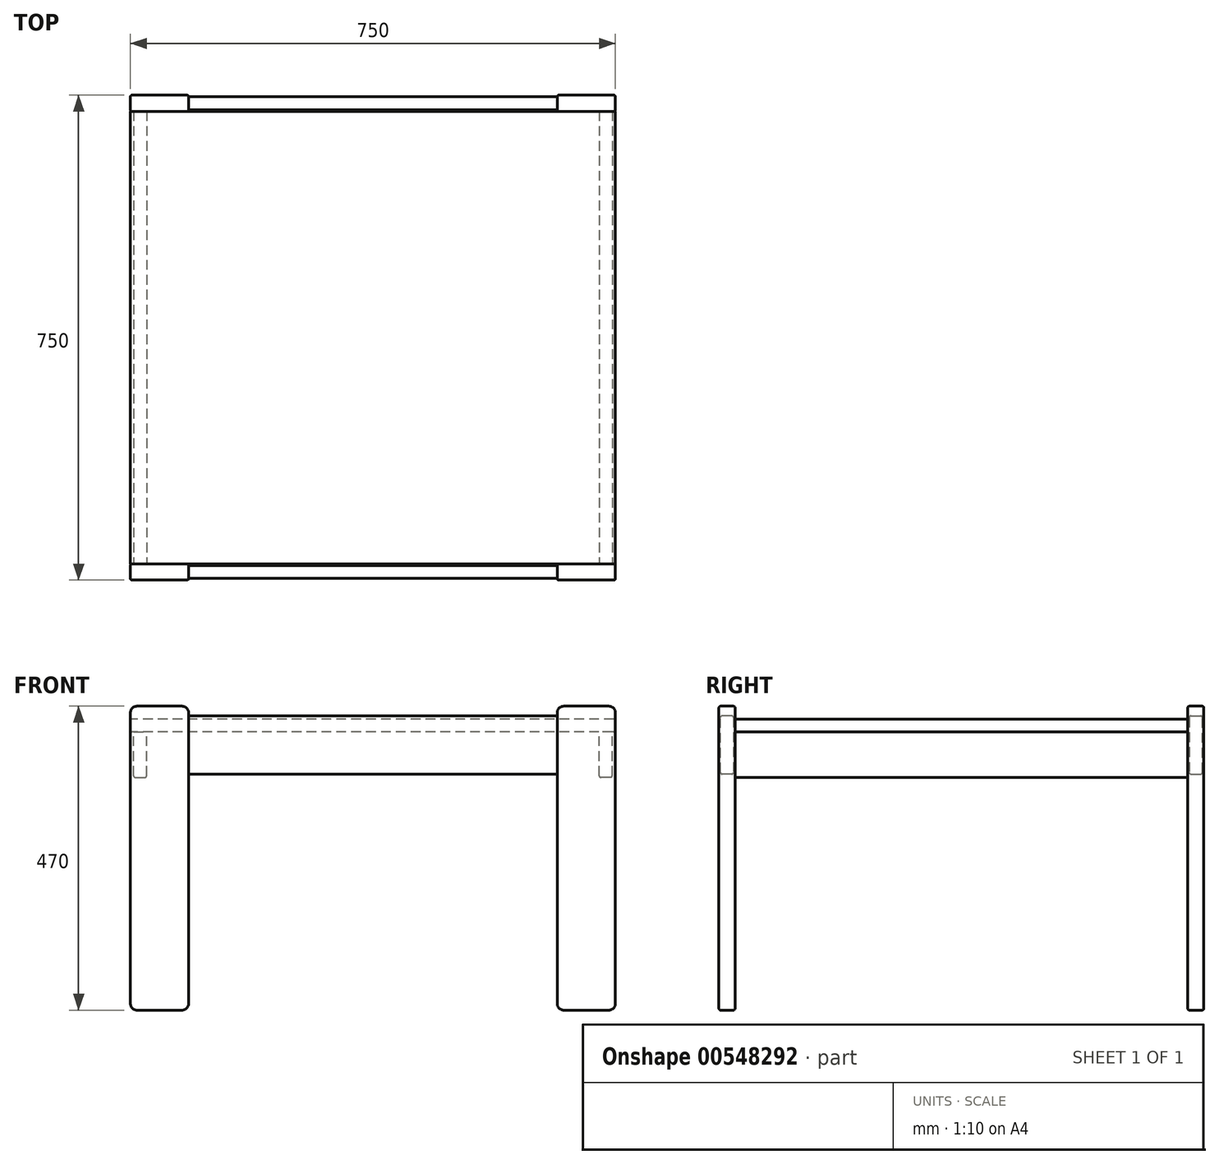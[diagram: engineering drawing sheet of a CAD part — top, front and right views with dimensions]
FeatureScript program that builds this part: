
annotation { "Feature Type Name" : "Feature", "Feature Type Description" : "" }
export const myFeature = defineFeature(function(context is Context, id is Id, definition is map)
    precondition{}
    {
        {
            var Q0;
            Q0=qCreatedBy(makeId("Top.planeOp"),FACE);
            var sketch = newSketch(context, id + "F0", { "sketchPlane" : qUnion([Q0])});
            skLineSegment(sketch, "E0.bottom", {"start": v(375, 350) * mm, "end": v(-375, 350) * mm});
            skLineSegment(sketch, "E0.top", {"start": v(375, -350) * mm, "end": v(-375, -350) * mm});
            skLineSegment(sketch, "E0.left", {"start": v(375, 350) * mm, "end": v(375, -350) * mm});
            skLineSegment(sketch, "E0.right", {"start": v(-375, 350) * mm, "end": v(-375, -350) * mm});
            skPoint(sketch, "E0.middle", {"position": v(0, 0) * mm});
            skSolve(sketch);
        }
        {
            var Q0;
            Q0 = qSketchRegion(id + "F0", true);
            extrude(context, id + "F1", {"entities" : qUnion([Q0]), "oppositeDirection" : true, "depth" : 20 * mm, "offsetDistance" : 25 * mm});
        }
        {
            var Q0;
            Q0=makeQuery(id+"F1.opExtrude","SWEPT_FACE",FACE,{"disambiguationData":[OSD([sQuery(id+"F0.wireOp",EDGE,"E0.top")])]});
            var sketch = newSketch(context, id + "F2", { "sketchPlane" : qUnion([Q0])});
            skLineSegment(sketch, "E1.bottom", {"start": v(375, 20) * mm, "end": v(285, 20) * mm});
            skLineSegment(sketch, "E1.top", {"start": v(375, -450) * mm, "end": v(285, -450) * mm});
            skLineSegment(sketch, "E1.left", {"start": v(375, 20) * mm, "end": v(375, -450) * mm});
            skLineSegment(sketch, "E1.right", {"start": v(285, 20) * mm, "end": v(285, -450) * mm});
            skSolve(sketch);
        }
        {
            var Q0;
            Q0 = qSketchRegion(id + "F2", true);
            extrude(context, id + "F3", {"entities" : qUnion([Q0]), "depth" : 25 * mm, "offsetDistance" : 25 * mm});
        }
        {
            var Q0;
            Q0=makeQuery(id+"F3.opExtrude","SWEPT_EDGE",EDGE,{"disambiguationData":[OSD([sQuery(id+"F2.wireOp",EDGE,"E1.bottom"),sQuery(id+"F2.wireOp",EDGE,"E1.left")])]});
            var Q1;
            Q1=makeQuery(id+"F3.opExtrude","SWEPT_EDGE",EDGE,{"disambiguationData":[OSD([sQuery(id+"F2.wireOp",EDGE,"E1.bottom"),sQuery(id+"F2.wireOp",EDGE,"E1.right")])]});
            var Q2;
            Q2=makeQuery(id+"F3.opExtrude","SWEPT_EDGE",EDGE,{"disambiguationData":[OSD([sQuery(id+"F2.wireOp",EDGE,"E1.top"),sQuery(id+"F2.wireOp",EDGE,"E1.left")])]});
            var Q3;
            Q3=makeQuery(id+"F3.opExtrude","SWEPT_EDGE",EDGE,{"disambiguationData":[OSD([sQuery(id+"F2.wireOp",EDGE,"E1.top"),sQuery(id+"F2.wireOp",EDGE,"E1.right")])]});
            fillet(context, id + "F4", {"entities" : qUnion([Q0, Q1, Q2, Q3]), "radius" : 10 * mm, "tangentPropagation" : true, "allowEdgeOverflow" : false});
        }
        {
            var Q0;
            Q0=makeQuery(id+"F3.opExtrude","CAP_FACE",FACE,{"disambiguationData":[OSD([sQuery(id+"F2.wireOp",EDGE,"E1.bottom"),sQuery(id+"F2.wireOp",EDGE,"E1.top"),sQuery(id+"F2.wireOp",EDGE,"E1.left"),sQuery(id+"F2.wireOp",EDGE,"E1.right")])],"isStart":true});
            var sketch = newSketch(context, id + "F5", { "sketchPlane" : qUnion([Q0])});
            skLineSegment(sketch, "E2.bottom", {"start": v(-370, -90) * mm, "end": v(-350, -90) * mm});
            skLineSegment(sketch, "E2.top", {"start": v(-370, -20) * mm, "end": v(-350, -20) * mm});
            skLineSegment(sketch, "E2.left", {"start": v(-370, -90) * mm, "end": v(-370, -20) * mm});
            skLineSegment(sketch, "E2.right", {"start": v(-350, -90) * mm, "end": v(-350, -20) * mm});
            skSolve(sketch);
        }
        {
            var Q0;
            Q0 = qSketchRegion(id + "F5", true);
            var Q1;
            Q1=makeQuery(id+"F1.opExtrude","SWEPT_FACE",FACE,{"disambiguationData":[OSD([sQuery(id+"F0.wireOp",EDGE,"E0.bottom")])]});
            extrude(context, id + "F6", {"entities" : qUnion([Q0]), "endBound" : BoundingType.UP_TO_SURFACE, "depth" : 25 * mm, "endBoundEntityFace" : qUnion([Q1]), "offsetDistance" : 25 * mm});
        }
        {
            var Q0;
            Q0=makeQuery(id+"F3.opExtrude","SWEPT_FACE",FACE,{"disambiguationData":[OSD([sQuery(id+"F2.wireOp",EDGE,"E1.bottom")])]});
            fillet(context, id + "F7", {"entities" : qUnion([Q0]), "radius" : 2.5 * mm, "tangentPropagation" : true, "allowEdgeOverflow" : false});
        }
        {
            var Q0;
            Q0=makeQuery(id+"F6.opExtrude","SWEPT_EDGE",EDGE,{"disambiguationData":[OSD([sQuery(id+"F5.wireOp",EDGE,"E2.bottom"),sQuery(id+"F5.wireOp",EDGE,"E2.right")])]});
            var Q1;
            Q1=makeQuery(id+"F6.opExtrude","SWEPT_EDGE",EDGE,{"disambiguationData":[OSD([sQuery(id+"F5.wireOp",EDGE,"E2.bottom"),sQuery(id+"F5.wireOp",EDGE,"E2.left")])]});
            fillet(context, id + "F8", {"entities" : qUnion([Q0, Q1]), "radius" : 2.5 * mm, "tangentPropagation" : true, "allowEdgeOverflow" : false});
        }
        {
            var Q0;
            Q0=makeQuery(id+"F3.opExtrude","SWEPT_BODY",BODY,{"disambiguationData":[OSD([sQuery(id+"F2.wireOp",EDGE,"E1.bottom"),sQuery(id+"F2.wireOp",EDGE,"E1.top"),sQuery(id+"F2.wireOp",EDGE,"E1.left"),sQuery(id+"F2.wireOp",EDGE,"E1.right")])]});
            var Q1;
            Q1=makeQuery(id+"F6.opExtrude","SWEPT_BODY",BODY,{"disambiguationData":[OSD([sQuery(id+"F5.wireOp",EDGE,"E2.bottom"),sQuery(id+"F5.wireOp",EDGE,"E2.top"),sQuery(id+"F5.wireOp",EDGE,"E2.left"),sQuery(id+"F5.wireOp",EDGE,"E2.right")])]});
            var Q2;
            Q2=qCreatedBy(makeId("Right.planeOp"),FACE);
            mirror(context, id + "F9", {"entities" : qUnion([Q0, Q1]), "mirrorPlane" : qUnion([Q2])});
        }
        {
            var Q0;
            Q0=makeQuery(id+"F3.opExtrude","SWEPT_FACE",FACE,{"disambiguationData":[OSD([sQuery(id+"F2.wireOp",EDGE,"E1.right")])]});
            var sketch = newSketch(context, id + "F10", { "sketchPlane" : qUnion([Q0])});
            skLineSegment(sketch, "E3.bottom", {"start": v(352.5, 5) * mm, "end": v(372.5, 5) * mm});
            skLineSegment(sketch, "E3.top", {"start": v(352.5, -85) * mm, "end": v(372.5, -85) * mm});
            skLineSegment(sketch, "E3.left", {"start": v(352.5, 5) * mm, "end": v(352.5, -85) * mm});
            skLineSegment(sketch, "E3.right", {"start": v(372.5, 5) * mm, "end": v(372.5, -85) * mm});
            skLineSegment(sketch, "E4", {"start": v(362.5, 5) * mm, "end": v(362.5, -85) * mm, "construction": true});
            skSolve(sketch);
        }
        {
            var Q0;
            Q0 = qSketchRegion(id + "F10", true);
            var Q1;
            Q1=makeQuery(id+"F9.opPattern","COPY",FACE,{"derivedFrom":makeQuery(id+"F3.opExtrude","SWEPT_FACE",FACE,{"disambiguationData":[OSD([sQuery(id+"F2.wireOp",EDGE,"E1.right")])]}),"instanceName":"1"});
            extrude(context, id + "F11", {"entities" : qUnion([Q0]), "endBound" : BoundingType.UP_TO_SURFACE, "depth" : 25 * mm, "endBoundEntityFace" : qUnion([Q1]), "offsetDistance" : 25 * mm});
        }
        {
            var Q0;
            Q0=makeQuery(id+"F11.opExtrude","SWEPT_EDGE",EDGE,{"disambiguationData":[OSD([sQuery(id+"F2.wireOp",EDGE,"E1.right"),sQuery(id+"F10.wireOp",EDGE,"E3.bottom"),sQuery(id+"F10.wireOp",EDGE,"E3.left")])]});
            var Q1;
            Q1=makeQuery(id+"F11.opExtrude","SWEPT_EDGE",EDGE,{"disambiguationData":[OSD([sQuery(id+"F2.wireOp",EDGE,"E1.right"),sQuery(id+"F10.wireOp",EDGE,"E3.bottom"),sQuery(id+"F10.wireOp",EDGE,"E3.right")])]});
            var Q2;
            Q2=makeQuery(id+"F11.opExtrude","SWEPT_EDGE",EDGE,{"disambiguationData":[OSD([sQuery(id+"F2.wireOp",EDGE,"E1.right"),sQuery(id+"F10.wireOp",EDGE,"E3.top"),sQuery(id+"F10.wireOp",EDGE,"E3.right")])]});
            var Q3;
            Q3=makeQuery(id+"F11.opExtrude","SWEPT_EDGE",EDGE,{"disambiguationData":[OSD([sQuery(id+"F2.wireOp",EDGE,"E1.right"),sQuery(id+"F10.wireOp",EDGE,"E3.top"),sQuery(id+"F10.wireOp",EDGE,"E3.left")])]});
            fillet(context, id + "F12", {"entities" : qUnion([Q0, Q1, Q2, Q3]), "radius" : 2.5 * mm, "tangentPropagation" : true, "allowEdgeOverflow" : false});
        }
        {
            var Q0;
            Q0=makeQuery(id+"F3.opExtrude","SWEPT_BODY",BODY,{"disambiguationData":[OSD([sQuery(id+"F2.wireOp",EDGE,"E1.bottom"),sQuery(id+"F2.wireOp",EDGE,"E1.top"),sQuery(id+"F2.wireOp",EDGE,"E1.left"),sQuery(id+"F2.wireOp",EDGE,"E1.right")])]});
            var Q1;
            Q1=makeQuery(id+"F9.opPattern","COPY",BODY,{"derivedFrom":makeQuery(id+"F3.opExtrude","SWEPT_BODY",BODY,{"disambiguationData":[OSD([sQuery(id+"F2.wireOp",EDGE,"E1.bottom"),sQuery(id+"F2.wireOp",EDGE,"E1.top"),sQuery(id+"F2.wireOp",EDGE,"E1.left"),sQuery(id+"F2.wireOp",EDGE,"E1.right")])]}),"instanceName":"1"});
            var Q2;
            Q2=makeQuery(id+"F11.opExtrude","SWEPT_BODY",BODY,{"disambiguationData":[OSD([sQuery(id+"F10.wireOp",EDGE,"E3.bottom"),sQuery(id+"F10.wireOp",EDGE,"E3.top"),sQuery(id+"F10.wireOp",EDGE,"E3.left"),sQuery(id+"F10.wireOp",EDGE,"E3.right")])]});
            var Q3;
            Q3=qCreatedBy(makeId("Front.planeOp"),FACE);
            mirror(context, id + "F13", {"entities" : qUnion([Q0, Q1, Q2]), "mirrorPlane" : qUnion([Q3])});
        }
        {
            var Q0;
            Q0=makeQuery(id+"F1.opExtrude","CAP_EDGE",EDGE,{"disambiguationData":[OSD([sQuery(id+"F0.wireOp",EDGE,"E0.left")])],"isStart":true});
            var Q1;
            Q1=makeQuery(id+"F1.opExtrude","CAP_EDGE",EDGE,{"disambiguationData":[OSD([sQuery(id+"F0.wireOp",EDGE,"E0.left")])],"isStart":false});
            var Q2;
            Q2=makeQuery(id+"F1.opExtrude","CAP_EDGE",EDGE,{"disambiguationData":[OSD([sQuery(id+"F0.wireOp",EDGE,"E0.right")])],"isStart":false});
            var Q3;
            Q3=makeQuery(id+"F1.opExtrude","CAP_EDGE",EDGE,{"disambiguationData":[OSD([sQuery(id+"F0.wireOp",EDGE,"E0.right")])],"isStart":true});
            fillet(context, id + "F14", {"entities" : qUnion([Q0, Q1, Q2, Q3]), "radius" : 2.5 * mm, "tangentPropagation" : true, "allowEdgeOverflow" : false});
        }
    });
